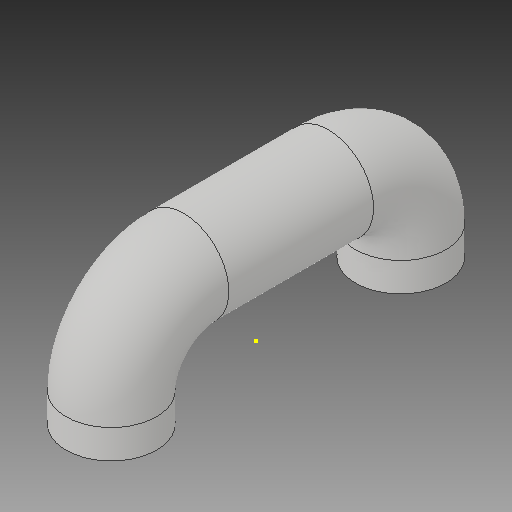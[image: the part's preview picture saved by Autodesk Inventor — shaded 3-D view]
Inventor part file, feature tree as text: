
AUTODESK INVENTOR PART (.ipt)
format: ipt  version: 2018 (Build 220112000, 112)  size: 147,968 bytes
history: native  units: mm
features: sketch x3, sweep x1
ambient origin geometry x8: Origin, YZ Plane, XZ Plane, XY Plane, X Axis, Y Axis, Z Axis, Center Point
bodies: Solid1 (feature_tree)
feature tree (4):
  sweep  "Sweep1"
  sketch  "Sketch3"  dims[d6=6.0mm d7=12.0mm d8=7.5mm d9=0.0mm d10=0.0mm]
  sketch  "Sketch1"  dims[d1=12.0mm d2=12.0mm]
  sketch  "Sketch2"  dims[d5=6.0mm]
